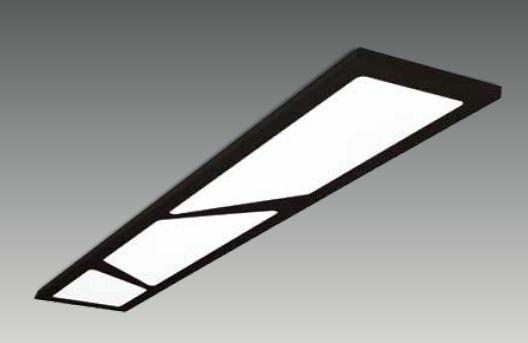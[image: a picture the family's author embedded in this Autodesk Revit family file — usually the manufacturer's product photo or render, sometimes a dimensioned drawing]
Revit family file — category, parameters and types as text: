
# Revit family: SK 3012 BRC-9
name_source: partatom
category: Lighting Fixtures
revit_build: Autodesk Revit 2016 (Build: 20150714_1515(x64)
units: mm (PartAtom-declared; Revit-internal decimal feet)

## family parameters
Always vertical = Yes
Cut with Voids When Loaded = No
Host = Ceiling
Light Source = Yes
OmniClass Number = 23.80.70.11
OmniClass Title = Luminaries for Internal Lighting
Part Type = Normal
Room Calculation Point = No
Round Connector Dimension = Use Diameter
Shared = No
Work Plane-Based = No

## types (2) — shared parameters
Color Filter = 16777215
Dimming Lamp Color Temperature Shift = <None>
Emit Shape Visible in Rendering = Yes
Emit from Rectangle Length = 1190 mm  [stored 3.9042 ft]
Emit from Rectangle Width = 290 mm  [stored 0.951444 ft]
Light Source Symbol Size = 610 mm
Manufacturer = ARLIGHT
Type Image = SK 3012 BRC.JPG
Wattage Comments = 39

## type names (no varying parameters)
- SKBRC.3012.39.30
- SKBRC.3012.39.40

note: [stored X ft] marks values corroborated as IEEE doubles in the binary element streams (Revit-internal decimal feet)

## geometry (parser evidence)
native form markers: Sweep x3
no freeform markers — native parametric forms only
